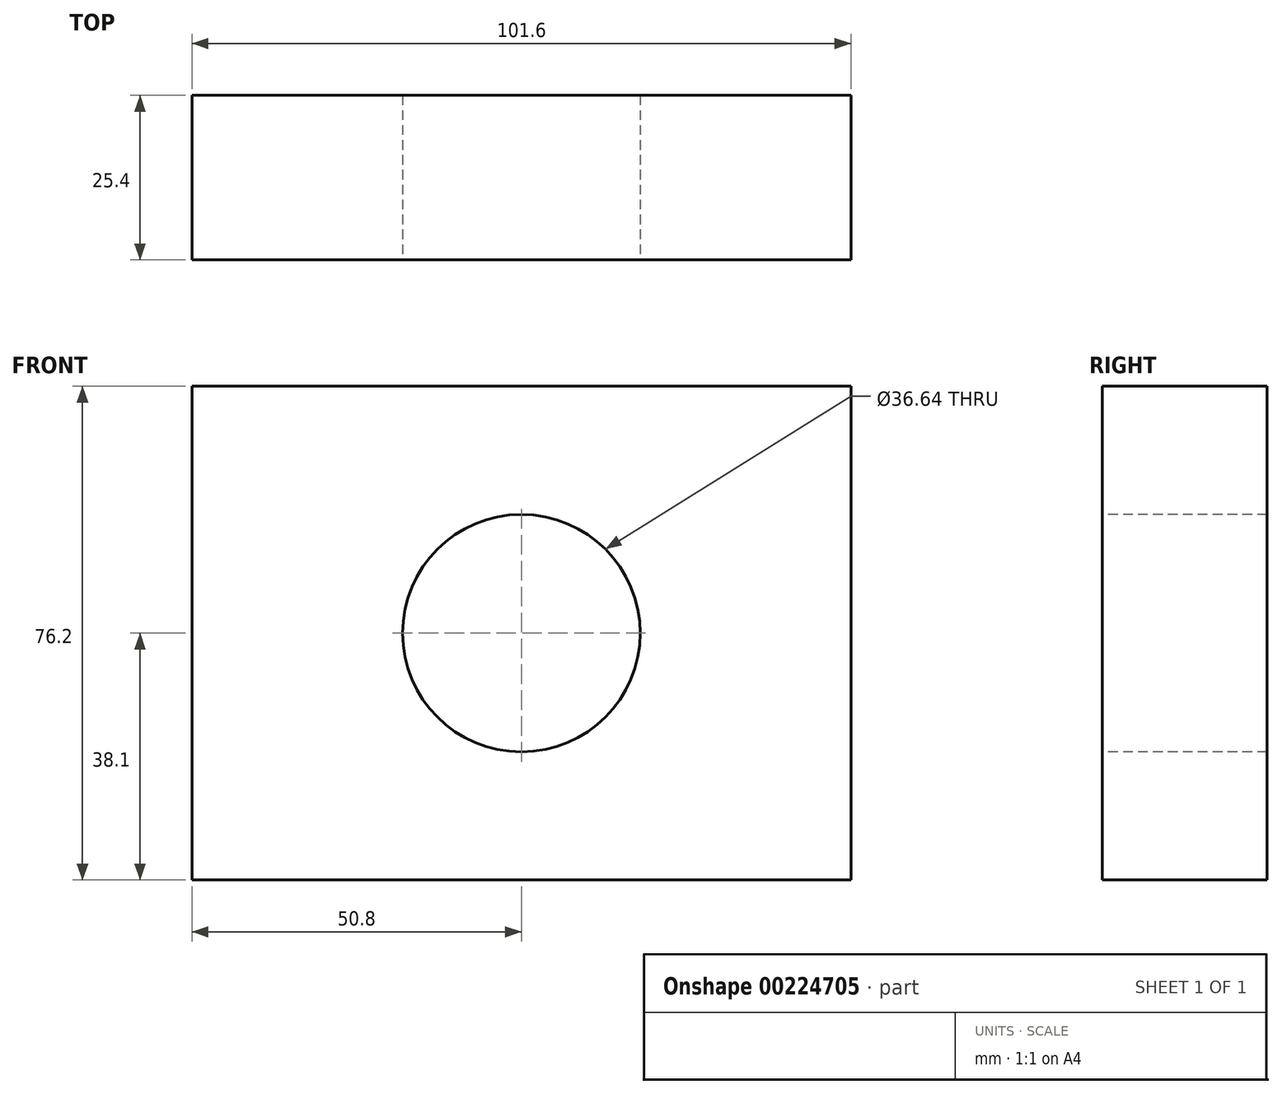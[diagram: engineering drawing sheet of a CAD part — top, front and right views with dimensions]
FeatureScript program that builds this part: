
annotation { "Feature Type Name" : "Feature", "Feature Type Description" : "" }
export const myFeature = defineFeature(function(context is Context, id is Id, definition is map)
    precondition{}
    {
        {
            var Q0;
            Q0=qCreatedBy(makeId("Front.planeOp"),FACE);
            var sketch = newSketch(context, id + "F0", { "sketchPlane" : qUnion([Q0])});
            skLineSegment(sketch, "E0.bottom", {"start": v(-50.8, 38.1) * mm, "end": v(50.8, 38.1) * mm});
            skLineSegment(sketch, "E0.top", {"start": v(-50.8, -38.1) * mm, "end": v(50.8, -38.1) * mm});
            skLineSegment(sketch, "E0.left", {"start": v(-50.8, 38.1) * mm, "end": v(-50.8, -38.1) * mm});
            skLineSegment(sketch, "E0.right", {"start": v(50.8, 38.1) * mm, "end": v(50.8, -38.1) * mm});
            skPoint(sketch, "E0.middle", {"position": v(0, 0) * mm});
            skSolve(sketch);
        }
        {
            var Q0;
            Q0 = qSketchRegion(id + "F0", true);
            extrude(context, id + "F1", {"entities" : qUnion([Q0]), "endBound" : BoundingType.SYMMETRIC, "depth" : 25.4 * mm});
        }
        {
            var Q0;
            Q0=makeQuery(id+"F1.opExtrude","CAP_FACE",FACE,{"disambiguationData":[OSD([sQuery(id+"F0.wireOp",EDGE,"E0.bottom"),sQuery(id+"F0.wireOp",EDGE,"E0.top"),sQuery(id+"F0.wireOp",EDGE,"E0.left"),sQuery(id+"F0.wireOp",EDGE,"E0.right")])],"isStart":false});
            var sketch = newSketch(context, id + "F2", { "sketchPlane" : qUnion([Q0])});
            skCircle(sketch, "E1", {"center": v(0, 0) * mm, "radius": 18.32 * mm});
            skSolve(sketch);
        }
        {
            var Q0;
            Q0 = qSketchRegion(id + "F2", true);
            extrude(context, id + "F3", {"entities" : qUnion([Q0]), "operationType" : NewBodyOperationType.REMOVE, "endBound" : BoundingType.THROUGH_ALL, "oppositeDirection" : true, "depth" : 25.4 * mm});
        }
    });
